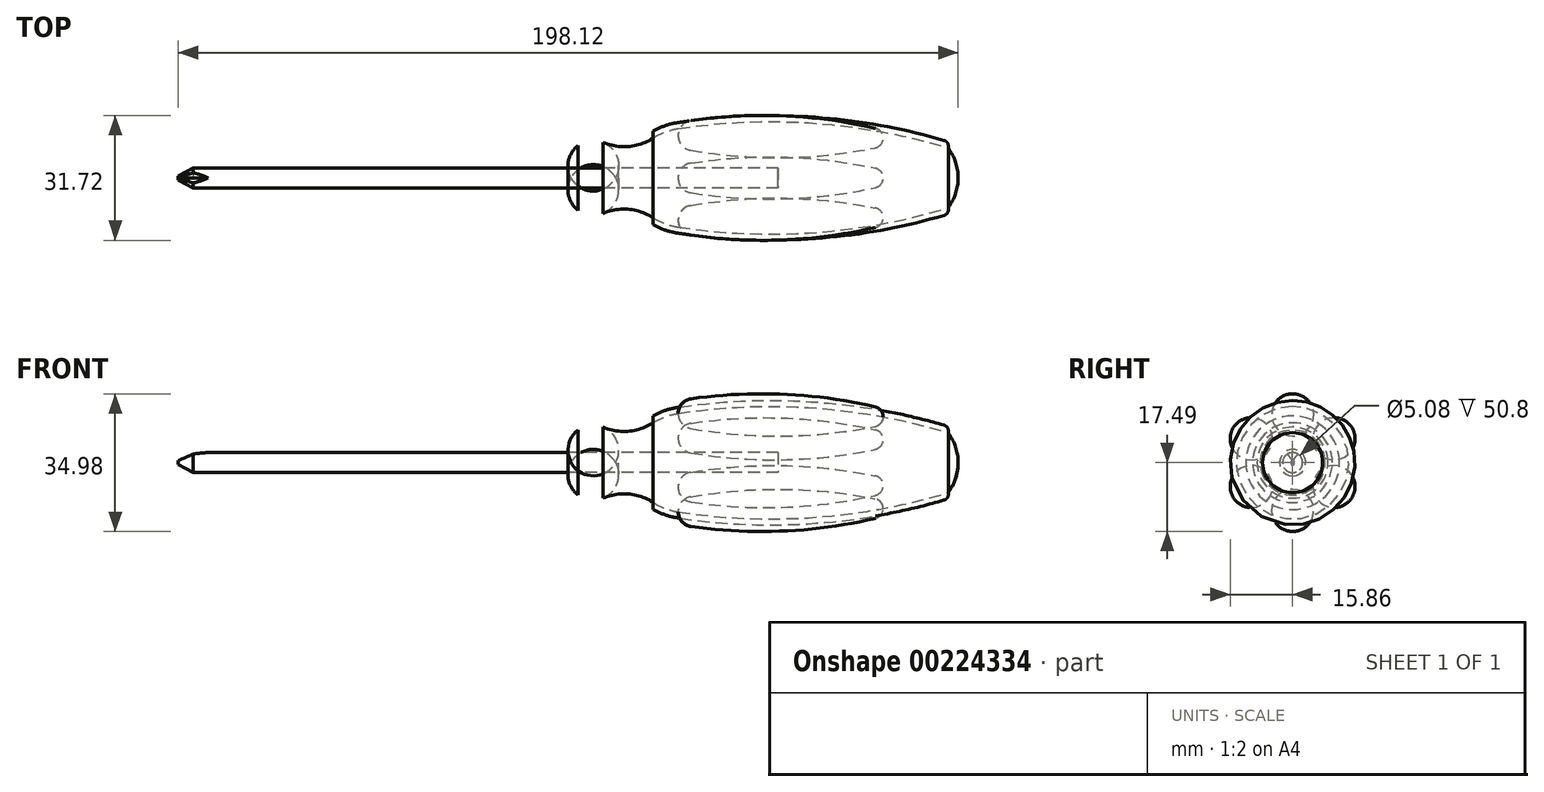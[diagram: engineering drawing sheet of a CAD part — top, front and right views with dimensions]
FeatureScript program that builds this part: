
annotation { "Feature Type Name" : "Feature", "Feature Type Description" : "" }
export const myFeature = defineFeature(function(context is Context, id is Id, definition is map)
    precondition{}
    {
        {
            var Q0;
            Q0=qCreatedBy(makeId("Front.planeOp"),FACE);
            var sketch = newSketch(context, id + "F0", { "sketchPlane" : qUnion([Q0])});
            skLineSegment(sketch, "E0", {"start": v(-101.6, 0) * mm, "end": v(96.52, 0) * mm});
            skLineSegment(sketch, "E1", {"start": v(96.52, 0) * mm, "end": v(117.55, 0) * mm, "construction": true});
            skLineSegment(sketch, "E2", {"start": v(50.8, 2.54) * mm, "end": v(-97.8, 2.54) * mm});
            skLineSegment(sketch, "E3", {"start": v(-101.6, 0.5) * mm, "end": v(-101.6, 0) * mm});
            skLineSegment(sketch, "E4", {"start": v(0, 2.54) * mm, "end": v(0, 8.25) * mm});
            skArc(sketch, "E5", {"start": v(6.35, 9.02) * mm, "mid": v(3.07, 9.48) * mm, "end": v(0, 8.25) * mm});
            skArc(sketch, "E6", {"start": v(6.35, 9.02) * mm, "mid": v(12.84, 7.99) * mm, "end": v(19.05, 10.11) * mm});
            skArc(sketch, "E7", {"start": v(25.4, 12.52) * mm, "mid": v(22.1, 11.65) * mm, "end": v(19.05, 10.11) * mm});
            skArc(sketch, "E8", {"start": v(93.98, 7.62) * mm, "mid": v(59.96, 13.9) * mm, "end": v(25.4, 12.52) * mm});
            skArc(sketch, "E9", {"start": v(96.52, 0) * mm, "mid": v(95.87, 4.02) * mm, "end": v(93.98, 7.62) * mm});
            skArc(sketch, "E10.0", {"start": v(25.17, 14.02) * mm, "mid": v(22.01, 13.24) * mm, "end": v(19.05, 11.9) * mm});
            skArc(sketch, "E10.1", {"start": v(92.95, 9.52) * mm, "mid": v(59.3, 15.46) * mm, "end": v(25.17, 14.02) * mm});
            skLineSegment(sketch, "E11", {"start": v(19.05, 11.9) * mm, "end": v(19.05, 10.11) * mm});
            skArc(sketch, "E12", {"start": v(93.98, 7.62) * mm, "mid": v(93.86, 8.78) * mm, "end": v(92.95, 9.52) * mm});
            skPoint(sketch, "E13.orphan", {"position": v(0, 0) * mm});
            skLineSegment(sketch, "E14", {"start": v(50.8, 2.54) * mm, "end": v(50.8, 0) * mm});
            skLineSegment(sketch, "E15", {"start": v(-101.6, 0.5) * mm, "end": v(-97.8, 2.54) * mm});
            skPoint(sketch, "E16.orphan", {"position": v(-101.6, 2.54) * mm});
            skSolve(sketch);
        }
        {
            var Q0;
            Q0=qCreatedBy(makeId("Front.planeOp"),FACE);
            var sketch = newSketch(context, id + "F1", { "sketchPlane" : qUnion([Q0])});
            skLineSegment(sketch, "E17", {"start": v(25.4, 12.52) * mm, "end": v(77.47, 11.64) * mm});
            skArc(sketch, "E18", {"start": v(28.67, 16.22) * mm, "mid": v(26.35, 14.97) * mm, "end": v(25.4, 12.52) * mm});
            skArc(sketch, "E19", {"start": v(77.47, 11.64) * mm, "mid": v(76.93, 13.25) * mm, "end": v(75.5, 14.16) * mm});
            skArc(sketch, "E20", {"start": v(75.5, 14.16) * mm, "mid": v(52.19, 17.37) * mm, "end": v(28.67, 16.22) * mm});
            skSolve(sketch);
        }
        {
            var Q0;
            Q0=qCreatedBy(makeId("Front.planeOp"),FACE);
            var sketch = newSketch(context, id + "F2", { "sketchPlane" : qUnion([Q0])});
            skLineSegment(sketch, "E21", {"start": v(-101.6, 0.5) * mm, "end": v(-93.98, 2.54) * mm});
            skSolve(sketch);
        }
        {
            var Q0;
            Q0=sQuery(id+"F2.wireOp",VERTEX,"E21.start");
            var Q1;
            Q1=sQuery(id+"F2.wireOp",EDGE,"E21");
            cPlane(context, id + "F3", {"entities" : qUnion([Q0, Q1]), "cplaneType" : CPlaneType.LINE_POINT, "offset" : 25.4 * mm, "width" : 152.4 * mm, "height" : 152.4 * mm});
        }
        {
            var Q0;
            Q0=qCreatedBy(id+"F3.planeOp",FACE);
            var sketch = newSketch(context, id + "F4", { "sketchPlane" : qUnion([Q0])});
            skLineSegment(sketch, "E22", {"start": v(5.08, 29.2) * mm, "end": v(0, 26.67) * mm});
            skLineSegment(sketch, "E23", {"start": v(0, 26.67) * mm, "end": v(-5.08, 29.2) * mm});
            skLineSegment(sketch, "E24", {"start": v(-5.08, 29.2) * mm, "end": v(5.08, 29.2) * mm});
            skLineSegment(sketch, "E25", {"start": v(0, 29.2) * mm, "end": v(0, 26.67) * mm, "construction": true});
            skSolve(sketch);
        }
        {
            var Q0;
            {var subQ0=sQuery(id+"F0.wireOp",EDGE,"E3");Q0=makeQuery(id+"F0.imprint","IMPRINT",FACE,{"disambiguationData":[TD([[makeQuery(id+"F0.imprint","IMPRINT",EDGE,{"derivedFrom":subQ0}),1.0]])]});}
            var Q1;
            Q1=sQuery(id+"F0.wireOp",EDGE,"E1");
            revolve(context, id + "F5", {"entities" : qUnion([Q0]), "axis" : qUnion([Q1]), "revolveType" : RevolveType.FULL});
        }
        {
            var Q0;
            {var subQ0=sQuery(id+"F0.wireOp",EDGE,"E4");Q0=makeQuery(id+"F0.imprint","IMPRINT",FACE,{"disambiguationData":[TD([[makeQuery(id+"F0.imprint","IMPRINT",EDGE,{"derivedFrom":subQ0}),-1.0]])]});}
            var Q1;
            Q1=sQuery(id+"F0.wireOp",EDGE,"E1");
            revolve(context, id + "F6", {"entities" : qUnion([Q0]), "axis" : qUnion([Q1]), "revolveType" : RevolveType.FULL});
        }
        {
            var Q0;
            Q0=makeQuery(id+"F0.imprint","IMPRINT",FACE,{"disambiguationData":[TD([[makeQuery(id+"F0.imprint","IMPRINT",EDGE,{"derivedFrom":sQuery(id+"F0.wireOp",EDGE,"E7")}),-1.0]])]});
            var Q1;
            Q1=sQuery(id+"F0.wireOp",EDGE,"E1");
            revolve(context, id + "F7", {"entities" : qUnion([Q0]), "axis" : qUnion([Q1]), "revolveType" : RevolveType.FULL});
        }
        {
            var Q0;
            Q0=makeQuery(id+"F1.imprint","IMPRINT",FACE,{"disambiguationData":[TD([[makeQuery(id+"F1.imprint","IMPRINT",EDGE,{"derivedFrom":sQuery(id+"F1.wireOp",EDGE,"E17")}),1.0]])]});
            var Q1;
            Q1=sQuery(id+"F1.wireOp",EDGE,"E17");
            revolve(context, id + "F8", {"entities" : qUnion([Q0]), "axis" : qUnion([Q1]), "revolveType" : RevolveType.FULL});
        }
        {
            var Q0;
            Q0=makeQuery(id+"F8.opRevolve","SWEPT_BODY",BODY,{"disambiguationData":[OSD([sQuery(id+"F1.wireOp",EDGE,"E17"),sQuery(id+"F1.wireOp",EDGE,"E18"),sQuery(id+"F1.wireOp",EDGE,"E19"),sQuery(id+"F1.wireOp",EDGE,"E20")])]});
            var Q1;
            Q1=sQuery(id+"F0.wireOp",EDGE,"E1");
            circularPattern(context, id + "F9", {"entities" : qUnion([Q0]), "axis" : qUnion([Q1]), "angle" : 360 * degree, "instanceCount" : 6, "equalSpace" : true});
        }
        {
            var Q0;
            Q0=makeQuery(id+"F6.opRevolve","SWEPT_BODY",BODY,{"disambiguationData":[OSD([sQuery(id+"F0.wireOp",EDGE,"E0"),sQuery(id+"F0.wireOp",EDGE,"E2"),sQuery(id+"F0.wireOp",EDGE,"E4"),sQuery(id+"F0.wireOp",EDGE,"E5"),sQuery(id+"F0.wireOp",EDGE,"E6"),sQuery(id+"F0.wireOp",EDGE,"E7"),sQuery(id+"F0.wireOp",EDGE,"E8"),sQuery(id+"F0.wireOp",EDGE,"E9"),sQuery(id+"F0.wireOp",EDGE,"E14")])]});
            var Q1;
            Q1=makeQuery(id+"F7.opRevolve","SWEPT_BODY",BODY,{"disambiguationData":[OSD([sQuery(id+"F0.wireOp",EDGE,"E7"),sQuery(id+"F0.wireOp",EDGE,"E8"),sQuery(id+"F0.wireOp",EDGE,"E10.0"),sQuery(id+"F0.wireOp",EDGE,"E10.1"),sQuery(id+"F0.wireOp",EDGE,"E11"),sQuery(id+"F0.wireOp",EDGE,"E12")])]});
            booleanBodies(context, id + "F10", {"operationType" : BooleanOperationType.SUBTRACTION, "tools" : qUnion([Q0]), "targets" : qUnion([Q1]), "keepTools" : true});
        }
        {
            var Q0;
            Q0=qSketchRegion(id+"F4",true);
            var Q1;
            Q1=qConstructionFilter(qBodyType(qCreatedBy(id+"F2",EDGE),BodyType.WIRE),ConstructionObject.NO);
            sweep(context, id + "F11", {"operationType" : NewBodyOperationType.REMOVE, "profiles" : qUnion([Q0]), "path" : qUnion([Q1])});
        }
    });
